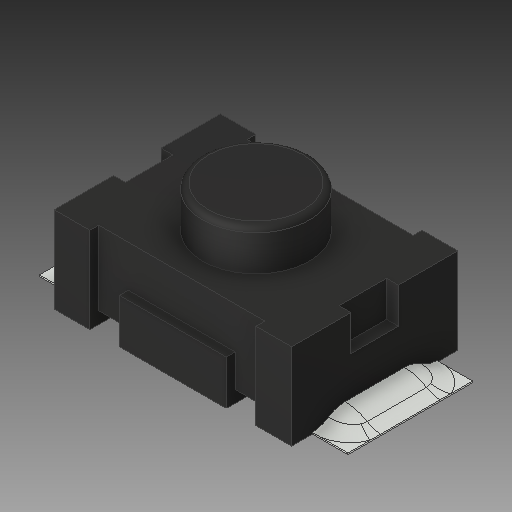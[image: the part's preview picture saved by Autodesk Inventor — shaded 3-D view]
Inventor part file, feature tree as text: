
AUTODESK INVENTOR PART (.ipt)
format: ipt  version: 2019 (Build 230136000, 136)  size: 210,944 bytes
history: native  units: in
note: dims shown in document units (in); Inventor stores cm internally (conversion verified against a paired STEP export)
features: fillet x1
ambient origin geometry x8: Origin, YZ Plane, XZ Plane, XY Plane, X Axis, Y Axis, Z Axis, Center Point
bodies: Solid1 (feature_tree)
feature tree (1):
  fillet  "Fillet3"  [1 undecoded]
note: 1 required parameter value undecoded (feature->parameter linkage not recoverable at this tier; creation-order binding heuristic only, values carry confidence <= 0.55)
